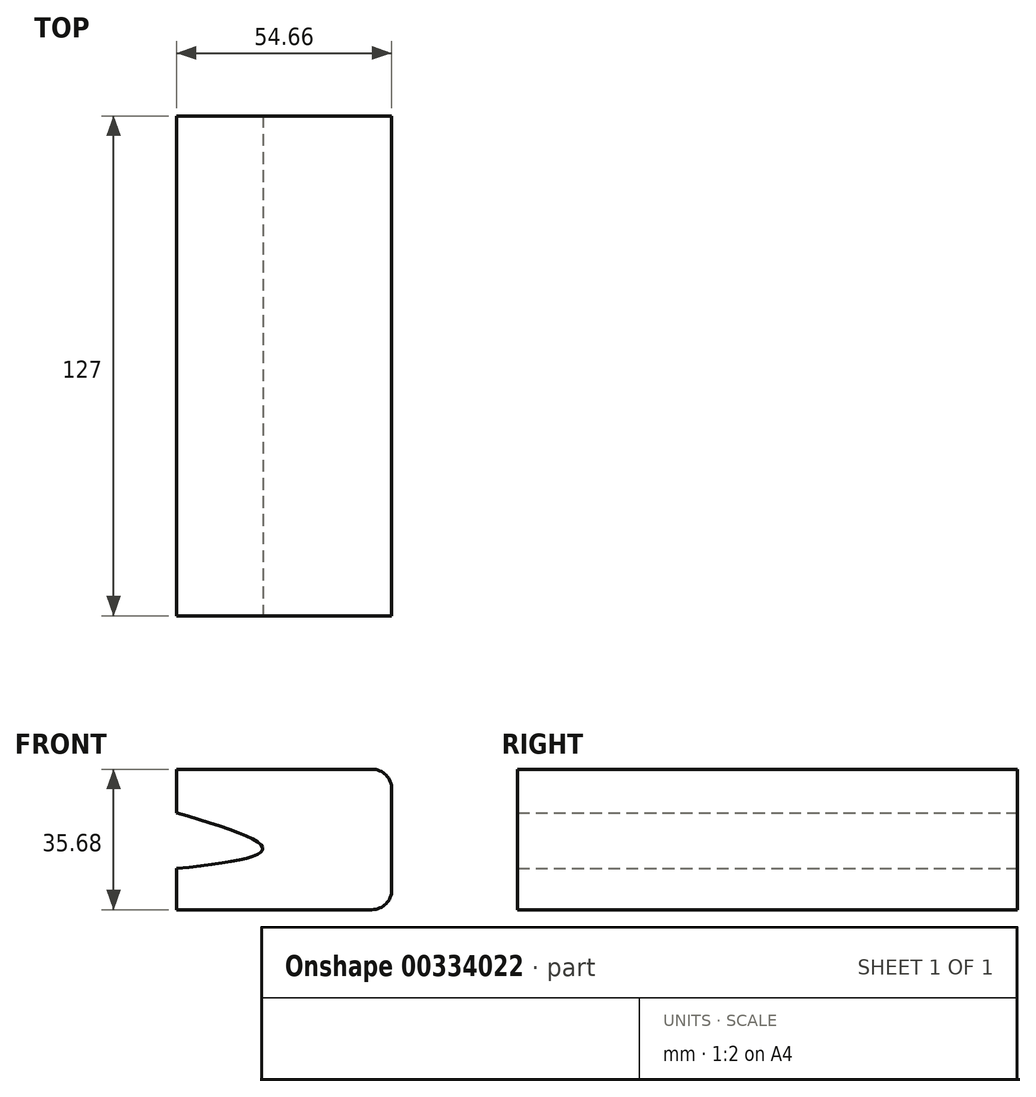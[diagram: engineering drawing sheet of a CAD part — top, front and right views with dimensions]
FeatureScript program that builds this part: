
annotation { "Feature Type Name" : "Feature", "Feature Type Description" : "" }
export const myFeature = defineFeature(function(context is Context, id is Id, definition is map)
    precondition{}
    {
        {
            var Q0;
            Q0=qCreatedBy(makeId("Front.planeOp"),FACE);
            var sketch = newSketch(context, id + "F0", { "sketchPlane" : qUnion([Q0])});
            skLineSegment(sketch, "E0.bottom", {"start": v(-33.02, 24.86) * mm, "end": v(42.9, 24.86) * mm});
            skLineSegment(sketch, "E0.top", {"start": v(-33.02, -22.59) * mm, "end": v(42.9, -22.59) * mm});
            skLineSegment(sketch, "E0.left", {"start": v(-33.02, 24.86) * mm, "end": v(-33.02, -22.59) * mm});
            skLineSegment(sketch, "E0.right", {"start": v(42.9, 24.86) * mm, "end": v(42.9, -22.59) * mm});
            skLineSegment(sketch, "E1.bottom", {"start": v(83.51, 68.52) * mm, "end": v(138.17, 68.52) * mm});
            skLineSegment(sketch, "E1.top", {"start": v(83.51, 32.84) * mm, "end": v(138.17, 32.84) * mm});
            skLineSegment(sketch, "E1.left", {"start": v(83.51, 68.52) * mm, "end": v(83.51, 32.84) * mm});
            skLineSegment(sketch, "E1.right", {"start": v(138.17, 68.52) * mm, "end": v(138.17, 32.84) * mm});
            skLineSegment(sketch, "E2", {"start": v(42.9, 24.86) * mm, "end": v(67.19, 41.95) * mm});
            skFitSpline(sketch, "E3", {"points": [v(67.19, 41.95) * mm, v(104.77, 49.54) * mm, v(67.19, 62.82) * mm, v(67.19, 63.2) * mm, v(-33.02, 24.86) * mm], "startDerivative": vector(240.13, 18.92) * mm, "endDerivative": vector(-339.52, -133.86) * mm});
            skSolve(sketch);
        }
        {
            var Q0;
            {var subQ4=sQuery(id+"F0.wireOp",EDGE,"E1.bottom");Q0=makeQuery(id+"F0.imprint","IMPRINT",FACE,{"disambiguationData":[TD([[makeQuery(id+"F0.imprint","IMPRINT",EDGE,{"derivedFrom":subQ4}),-1.0]])]});}
            extrude(context, id + "F1", {"entities" : qUnion([Q0]), "endBound" : BoundingType.SYMMETRIC, "depth" : 127 * mm});
        }
        {
            var Q0;
            Q0=makeQuery(id+"F1.opExtrude","SWEPT_EDGE",EDGE,{"disambiguationData":[OSD([sQuery(id+"F0.wireOp",EDGE,"E1.top"),sQuery(id+"F0.wireOp",EDGE,"E1.right")])]});
            var Q1;
            Q1=makeQuery(id+"F1.opExtrude","SWEPT_EDGE",EDGE,{"disambiguationData":[OSD([sQuery(id+"F0.wireOp",EDGE,"E1.bottom"),sQuery(id+"F0.wireOp",EDGE,"E1.right")])]});
            fillet(context, id + "F2", {"entities" : qUnion([Q0, Q1]), "radius" : 5.08 * mm, "tangentPropagation" : true, "allowEdgeOverflow" : false});
        }
    });
